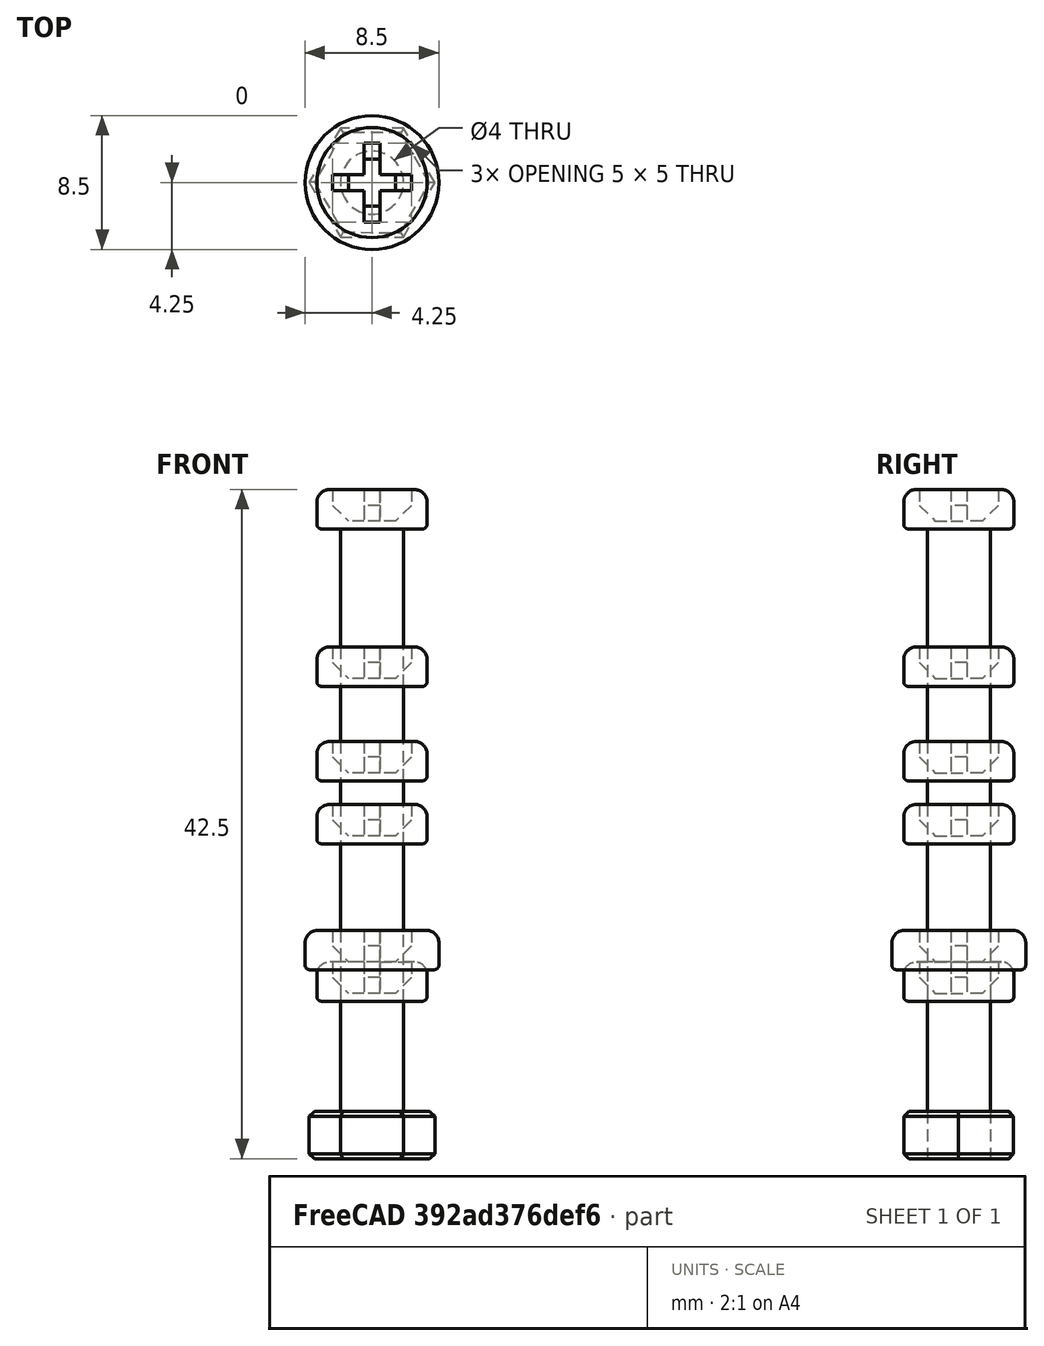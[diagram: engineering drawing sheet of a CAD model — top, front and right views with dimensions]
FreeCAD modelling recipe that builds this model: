
FCSTD DOCUMENT  (FreeCAD 0.18R4 (GitTag))
Label: M4_Screw
License: All rights reserved
LicenseURL: http://en.wikipedia.org/wiki/All_rights_reserved
objects: Sketcher::SketchObject×25, PartDesign::Pad×13, PartDesign::Pocket×12, PartDesign::Fillet×12, PartDesign::Chamfer×8, PartDesign::Body×7
note: 102 computed .brp shape members not serialized (recipe doc carries the construction recipe); baked Part::Feature solids carry a one-line shape summary decoded from their .brp

FEATURE [Sketcher::SketchObject] Sketch
  MapMode = 5
  Support = -> [XY_Plane]
  sketch-geometry (1):
    g0: Circle CenterX=0 CenterY=0 CenterZ=0 NormalX=0 NormalY=0 NormalZ=1 AngleXU=0 Radius=2
  constraints (2):
    c: Coincident(g0,g-1)
    c: Diameter(g0) = 4
FEATURE [PartDesign::Pad] Pad
  Length = 10
  Length2 = 100
  Profile = -> Sketch
  Type = 0
FEATURE [Sketcher::SketchObject] Sketch001
  MapMode = 5
  Placement = pos=(0,0,10) rot=(0,0,1;0rad)
  Support = -> [Pad]
  sketch-geometry (1):
    g0: Circle CenterX=0 CenterY=0 CenterZ=0 NormalX=0 NormalY=0 NormalZ=1 AngleXU=0 Radius=3.5
  constraints (2):
    c: Diameter(g0) = 7
    c: Coincident(g0,g-1)
FEATURE [PartDesign::Pad] Pad001
  BaseFeature = -> Pad
  Length = 2.5
  Length2 = 100
  Profile = -> Sketch001
  Type = 0
FEATURE [Sketcher::SketchObject] Sketch002
  MapMode = 5
  Placement = pos=(0,0,12.5) rot=(0,0,1;0rad)
  Support = -> [Pad001]
  sketch-geometry (4):
    g0: LineSegment StartX=-2.5 StartY=0.5 StartZ=0 EndX=2.5 EndY=0.5 EndZ=0
    g1: LineSegment StartX=2.5 StartY=0.5 StartZ=0 EndX=2.5 EndY=-0.5 EndZ=0
    g2: LineSegment StartX=2.5 StartY=-0.5 StartZ=0 EndX=-2.5 EndY=-0.5 EndZ=0
    g3: LineSegment StartX=-2.5 StartY=-0.5 StartZ=0 EndX=-2.5 EndY=0.5 EndZ=0
  constraints (12):
    c: Coincident(g0,g1)
    c: Coincident(g1,g2)
    c: Coincident(g2,g3)
    c: Coincident(g3,g0)
    c: Horizontal(g0)
    c: Horizontal(g2)
    c: Vertical(g1)
    c: Vertical(g3)
    c: Distance(g1) = 1
    c: Distance(g0) = 5
    c: Distance(g0,g-2) = 2.5
    c: Distance(g0,g-1) = 0.5
FEATURE [PartDesign::Pocket] Pocket
  BaseFeature = -> Pad001
  Length = 2
  Length2 = 100
  Profile = -> Sketch002
  Type = 0
FEATURE [Sketcher::SketchObject] Sketch003
  MapMode = 5
  Placement = pos=(0,0,12.5) rot=(0,0,1;0rad)
  Support = -> [Pocket]
  sketch-geometry (4):
    g0: LineSegment StartX=-0.5 StartY=2.5 StartZ=0 EndX=0.5 EndY=2.5 EndZ=0
    g1: LineSegment StartX=0.5 StartY=2.5 StartZ=0 EndX=0.5 EndY=-2.5 EndZ=0
    g2: LineSegment StartX=0.5 StartY=-2.5 StartZ=0 EndX=-0.5 EndY=-2.5 EndZ=0
    g3: LineSegment StartX=-0.5 StartY=-2.5 StartZ=0 EndX=-0.5 EndY=2.5 EndZ=0
  constraints (12):
    c: Coincident(g0,g1)
    c: Coincident(g1,g2)
    c: Coincident(g2,g3)
    c: Coincident(g3,g0)
    c: Horizontal(g0)
    c: Horizontal(g2)
    c: Vertical(g1)
    c: Vertical(g3)
    c: Distance(g0) = 1
    c: Distance(g1) = 5
    c: Distance(g0,g-1) = 2.5
    c: Distance(g0,g-2) = 0.5
FEATURE [PartDesign::Pocket] Pocket001
  BaseFeature = -> Pocket
  Length = 2
  Length2 = 100
  Profile = -> Sketch003
  Type = 0
FEATURE [PartDesign::Fillet] Fillet
  Base = -> Pocket001 [Edge3]
  BaseFeature = -> Pocket001
  Radius = 0.8
FEATURE [PartDesign::Chamfer] Chamfer
  Base = -> Fillet [Edge33,Edge39,Edge44,Edge27]
  BaseFeature = -> Fillet
  Size = 1
FEATURE [PartDesign::Fillet] Fillet001
  Base = -> Chamfer [Edge55]
  BaseFeature = -> Chamfer
  Radius = 0.3
FEATURE [PartDesign::Body] Body  label="M4_10mm"
  Group = -> [Sketch,Pad,Sketch001,Pad001,Sketch002,Pocket,Sketch003,Pocket001,Fillet,Chamfer,Fillet001]
  Origin = -> Origin
  Tip = -> Fillet001
FEATURE [Sketcher::SketchObject] Sketch004
  MapMode = 5
  Support = -> [XY_Plane001]
  sketch-geometry (8):
    g0: LineSegment StartX=2.01275 StartY=3.45671 StartZ=0 EndX=-1.98722 EndY=3.47145 EndZ=0
    g1: LineSegment StartX=-1.98722 StartY=3.47145 StartZ=0 EndX=-3.99997 EndY=0.0147426 EndZ=0
    g2: LineSegment StartX=-3.99997 StartY=0.0147426 StartZ=0 EndX=-2.01275 EndY=-3.45671 EndZ=0
    g3: LineSegment StartX=-2.01275 StartY=-3.45671 StartZ=0 EndX=1.98722 EndY=-3.47145 EndZ=0
    g4: LineSegment StartX=1.98722 StartY=-3.47145 StartZ=0 EndX=3.99997 EndY=-0.0147426 EndZ=0
    g5: LineSegment StartX=3.99997 StartY=-0.0147426 StartZ=0 EndX=2.01275 EndY=3.45671 EndZ=0
    g6: Circle [constr] CenterX=0 CenterY=0 CenterZ=0 NormalX=0 NormalY=0 NormalZ=1 AngleXU=0 Radius=4
    g7: Circle CenterX=0 CenterY=0 CenterZ=0 NormalX=0 NormalY=0 NormalZ=1 AngleXU=0 Radius=2
  constraints (17):
    c: Coincident(g0,g1)
    c: Coincident(g1,g2)
    c: Coincident(g2,g3)
    c: Coincident(g3,g4)
    c: Coincident(g4,g5)
    c: Coincident(g5,g0)
    c: Equal(g0, g1-g5) x5
    c: PointOnObject(g0,g6)
    c: PointOnObject(g1,g6)
    c: PointOnObject(g2,g6)
    c: PointOnObject(g3,g6)
    c: PointOnObject(g4,g6)
    c: PointOnObject(g5,g6)
    c: Distance(g0) = 4
    c: Coincident(g6,g-1)
    c: Diameter(g7) = 4
    c: Coincident(g7,g-1)
FEATURE [PartDesign::Pad] Pad002
  Length = 3
  Length2 = 100
  Profile = -> Sketch004
  Type = 0
FEATURE [PartDesign::Chamfer] Chamfer001
  Base = -> Pad002 [Edge9,Edge12,Edge15,Edge17,Edge3,Edge6]
  BaseFeature = -> Pad002
  Size = 0.3
FEATURE [PartDesign::Chamfer] Chamfer002
  Base = -> Chamfer001 [Edge13,Edge12,Edge11,Edge3,Edge7,Edge14]
  BaseFeature = -> Chamfer001
  Size = 0.3
FEATURE [PartDesign::Body] Body001  label="M4_Nut"
  Group = -> [Sketch004,Pad002,Chamfer001,Chamfer002]
  Origin = -> Origin001
  Tip = -> Chamfer002
FEATURE [Sketcher::SketchObject] Sketch006
  MapMode = 5
  Support = -> [XY_Plane002]
  sketch-geometry (1):
    g0: Circle CenterX=0 CenterY=0 CenterZ=0 NormalX=0 NormalY=0 NormalZ=1 AngleXU=0 Radius=2
  constraints (2):
    c: Coincident(g0,g-1)
    c: Diameter(g0) = 4
FEATURE [PartDesign::Pad] Pad004
  Length = 30
  Length2 = 100
  Profile = -> Sketch006
  Type = 0
FEATURE [Sketcher::SketchObject] Sketch005
  MapMode = 5
  Placement = pos=(0,0,30) rot=(0,0,1;0rad)
  Support = -> [Pad004]
  sketch-geometry (1):
    g0: Circle CenterX=0 CenterY=0 CenterZ=0 NormalX=0 NormalY=0 NormalZ=1 AngleXU=0 Radius=3.5
  constraints (2):
    c: Diameter(g0) = 7
    c: Coincident(g0,g-1)
FEATURE [PartDesign::Pad] Pad003
  BaseFeature = -> Pad004
  Length = 2.5
  Length2 = 100
  Profile = -> Sketch005
  Type = 0
FEATURE [Sketcher::SketchObject] Sketch008
  MapMode = 5
  Placement = pos=(0,0,32.5) rot=(0,0,1;0rad)
  Support = -> [Pad003]
  sketch-geometry (4):
    g0: LineSegment StartX=-2.5 StartY=0.5 StartZ=0 EndX=2.5 EndY=0.5 EndZ=0
    g1: LineSegment StartX=2.5 StartY=0.5 StartZ=0 EndX=2.5 EndY=-0.5 EndZ=0
    g2: LineSegment StartX=2.5 StartY=-0.5 StartZ=0 EndX=-2.5 EndY=-0.5 EndZ=0
    g3: LineSegment StartX=-2.5 StartY=-0.5 StartZ=0 EndX=-2.5 EndY=0.5 EndZ=0
  constraints (12):
    c: Coincident(g0,g1)
    c: Coincident(g1,g2)
    c: Coincident(g2,g3)
    c: Coincident(g3,g0)
    c: Horizontal(g0)
    c: Horizontal(g2)
    c: Vertical(g1)
    c: Vertical(g3)
    c: Distance(g1) = 1
    c: Distance(g0) = 5
    c: Distance(g0,g-2) = 2.5
    c: Distance(g0,g-1) = 0.5
FEATURE [PartDesign::Pocket] Pocket003
  BaseFeature = -> Pad003
  Length = 2
  Length2 = 100
  Profile = -> Sketch008
  Type = 0
FEATURE [Sketcher::SketchObject] Sketch007
  MapMode = 5
  Placement = pos=(0,0,32.5) rot=(0,0,1;0rad)
  Support = -> [Pocket003]
  sketch-geometry (4):
    g0: LineSegment StartX=-0.5 StartY=2.5 StartZ=0 EndX=0.5 EndY=2.5 EndZ=0
    g1: LineSegment StartX=0.5 StartY=2.5 StartZ=0 EndX=0.5 EndY=-2.5 EndZ=0
    g2: LineSegment StartX=0.5 StartY=-2.5 StartZ=0 EndX=-0.5 EndY=-2.5 EndZ=0
    g3: LineSegment StartX=-0.5 StartY=-2.5 StartZ=0 EndX=-0.5 EndY=2.5 EndZ=0
  constraints (12):
    c: Coincident(g0,g1)
    c: Coincident(g1,g2)
    c: Coincident(g2,g3)
    c: Coincident(g3,g0)
    c: Horizontal(g0)
    c: Horizontal(g2)
    c: Vertical(g1)
    c: Vertical(g3)
    c: Distance(g0) = 1
    c: Distance(g1) = 5
    c: Distance(g0,g-1) = 2.5
    c: Distance(g0,g-2) = 0.5
FEATURE [PartDesign::Pocket] Pocket002
  BaseFeature = -> Pocket003
  Length = 2
  Length2 = 100
  Profile = -> Sketch007
  Type = 0
FEATURE [PartDesign::Fillet] Fillet003
  Base = -> Pocket002 [Edge3]
  BaseFeature = -> Pocket002
  Radius = 0.8
FEATURE [PartDesign::Chamfer] Chamfer003
  Base = -> Fillet003 [Edge33,Edge39,Edge44,Edge27]
  BaseFeature = -> Fillet003
  Size = 1
FEATURE [PartDesign::Fillet] Fillet002
  Base = -> Chamfer003 [Edge55]
  BaseFeature = -> Chamfer003
  Radius = 0.3
FEATURE [PartDesign::Body] Body002  label="M4_30mm"
  Group = -> [Sketch006,Pad004,Sketch005,Pad003,Sketch008,Pocket003,Sketch007,Pocket002,Fillet003,Chamfer003,Fillet002]
  Origin = -> Origin002
  Tip = -> Fillet002
FEATURE [Sketcher::SketchObject] Sketch010
  MapMode = 5
  Support = -> [XY_Plane003]
  sketch-geometry (1):
    g0: Circle CenterX=0 CenterY=0 CenterZ=0 NormalX=0 NormalY=0 NormalZ=1 AngleXU=0 Radius=2
  constraints (2):
    c: Coincident(g0,g-1)
    c: Diameter(g0) = 4
FEATURE [PartDesign::Pad] Pad006
  Length = 24
  Length2 = 100
  Profile = -> Sketch010
  Type = 0
FEATURE [Sketcher::SketchObject] Sketch009
  MapMode = 5
  Placement = pos=(0,0,24) rot=(0,0,1;0rad)
  Support = -> [Pad006]
  sketch-geometry (1):
    g0: Circle CenterX=0 CenterY=0 CenterZ=0 NormalX=0 NormalY=0 NormalZ=1 AngleXU=0 Radius=3.5
  constraints (2):
    c: Diameter(g0) = 7
    c: Coincident(g0,g-1)
FEATURE [PartDesign::Pad] Pad005
  BaseFeature = -> Pad006
  Length = 2.5
  Length2 = 100
  Profile = -> Sketch009
  Type = 0
FEATURE [Sketcher::SketchObject] Sketch012
  MapMode = 5
  Placement = pos=(0,0,26.5) rot=(0,0,1;0rad)
  Support = -> [Pad005]
  sketch-geometry (4):
    g0: LineSegment StartX=-2.5 StartY=0.5 StartZ=0 EndX=2.5 EndY=0.5 EndZ=0
    g1: LineSegment StartX=2.5 StartY=0.5 StartZ=0 EndX=2.5 EndY=-0.5 EndZ=0
    g2: LineSegment StartX=2.5 StartY=-0.5 StartZ=0 EndX=-2.5 EndY=-0.5 EndZ=0
    g3: LineSegment StartX=-2.5 StartY=-0.5 StartZ=0 EndX=-2.5 EndY=0.5 EndZ=0
  constraints (12):
    c: Coincident(g0,g1)
    c: Coincident(g1,g2)
    c: Coincident(g2,g3)
    c: Coincident(g3,g0)
    c: Horizontal(g0)
    c: Horizontal(g2)
    c: Vertical(g1)
    c: Vertical(g3)
    c: Distance(g1) = 1
    c: Distance(g0) = 5
    c: Distance(g0,g-2) = 2.5
    c: Distance(g0,g-1) = 0.5
FEATURE [PartDesign::Pocket] Pocket005
  BaseFeature = -> Pad005
  Length = 2
  Length2 = 100
  Profile = -> Sketch012
  Type = 0
FEATURE [Sketcher::SketchObject] Sketch011
  MapMode = 5
  Placement = pos=(0,0,26.5) rot=(0,0,1;0rad)
  Support = -> [Pocket005]
  sketch-geometry (4):
    g0: LineSegment StartX=-0.5 StartY=2.5 StartZ=0 EndX=0.5 EndY=2.5 EndZ=0
    g1: LineSegment StartX=0.5 StartY=2.5 StartZ=0 EndX=0.5 EndY=-2.5 EndZ=0
    g2: LineSegment StartX=0.5 StartY=-2.5 StartZ=0 EndX=-0.5 EndY=-2.5 EndZ=0
    g3: LineSegment StartX=-0.5 StartY=-2.5 StartZ=0 EndX=-0.5 EndY=2.5 EndZ=0
  constraints (12):
    c: Coincident(g0,g1)
    c: Coincident(g1,g2)
    c: Coincident(g2,g3)
    c: Coincident(g3,g0)
    c: Horizontal(g0)
    c: Horizontal(g2)
    c: Vertical(g1)
    c: Vertical(g3)
    c: Distance(g0) = 1
    c: Distance(g1) = 5
    c: Distance(g0,g-1) = 2.5
    c: Distance(g0,g-2) = 0.5
FEATURE [PartDesign::Pocket] Pocket004
  BaseFeature = -> Pocket005
  Length = 2
  Length2 = 100
  Profile = -> Sketch011
  Type = 0
FEATURE [PartDesign::Fillet] Fillet005
  Base = -> Pocket004 [Edge3]
  BaseFeature = -> Pocket004
  Radius = 0.8
FEATURE [PartDesign::Chamfer] Chamfer004
  Base = -> Fillet005 [Edge33,Edge39,Edge44,Edge27]
  BaseFeature = -> Fillet005
  Size = 1
FEATURE [PartDesign::Fillet] Fillet004
  Base = -> Chamfer004 [Edge55]
  BaseFeature = -> Chamfer004
  Radius = 0.3
FEATURE [PartDesign::Body] Body003  label="M4_24mm"
  Group = -> [Sketch010,Pad006,Sketch009,Pad005,Sketch012,Pocket005,Sketch011,Pocket004,Fillet005,Chamfer004,Fillet004]
  Origin = -> Origin003
  Tip = -> Fillet004
FEATURE [Sketcher::SketchObject] Sketch013
  MapMode = 5
  Support = -> [XY_Plane004]
  sketch-geometry (1):
    g0: Circle CenterX=0 CenterY=0 CenterZ=0 NormalX=0 NormalY=0 NormalZ=1 AngleXU=0 Radius=2
  constraints (2):
    c: Coincident(g0,g-1)
    c: Diameter(g0) = 4
FEATURE [PartDesign::Pad] Pad008
  Length = 40
  Length2 = 100
  Profile = -> Sketch013
  Type = 0
FEATURE [Sketcher::SketchObject] Sketch014
  MapMode = 5
  Placement = pos=(0,0,40) rot=(0,0,1;0rad)
  Support = -> [Pad008]
  sketch-geometry (1):
    g0: Circle CenterX=0 CenterY=0 CenterZ=0 NormalX=0 NormalY=0 NormalZ=1 AngleXU=0 Radius=3.5
  constraints (2):
    c: Diameter(g0) = 7
    c: Coincident(g0,g-1)
FEATURE [PartDesign::Pad] Pad007
  BaseFeature = -> Pad008
  Length = 2.5
  Length2 = 100
  Profile = -> Sketch014
  Type = 0
FEATURE [Sketcher::SketchObject] Sketch016
  MapMode = 5
  Placement = pos=(0,0,42.5) rot=(0,0,1;0rad)
  Support = -> [Pad007]
  sketch-geometry (4):
    g0: LineSegment StartX=-2.5 StartY=0.5 StartZ=0 EndX=2.5 EndY=0.5 EndZ=0
    g1: LineSegment StartX=2.5 StartY=0.5 StartZ=0 EndX=2.5 EndY=-0.5 EndZ=0
    g2: LineSegment StartX=2.5 StartY=-0.5 StartZ=0 EndX=-2.5 EndY=-0.5 EndZ=0
    g3: LineSegment StartX=-2.5 StartY=-0.5 StartZ=0 EndX=-2.5 EndY=0.5 EndZ=0
  constraints (12):
    c: Coincident(g0,g1)
    c: Coincident(g1,g2)
    c: Coincident(g2,g3)
    c: Coincident(g3,g0)
    c: Horizontal(g0)
    c: Horizontal(g2)
    c: Vertical(g1)
    c: Vertical(g3)
    c: Distance(g1) = 1
    c: Distance(g0) = 5
    c: Distance(g0,g-2) = 2.5
    c: Distance(g0,g-1) = 0.5
FEATURE [PartDesign::Pocket] Pocket006
  BaseFeature = -> Pad007
  Length = 2
  Length2 = 100
  Profile = -> Sketch016
  Type = 0
FEATURE [Sketcher::SketchObject] Sketch015
  MapMode = 5
  Placement = pos=(0,0,42.5) rot=(0,0,1;0rad)
  Support = -> [Pocket006]
  sketch-geometry (4):
    g0: LineSegment StartX=-0.5 StartY=2.5 StartZ=0 EndX=0.5 EndY=2.5 EndZ=0
    g1: LineSegment StartX=0.5 StartY=2.5 StartZ=0 EndX=0.5 EndY=-2.5 EndZ=0
    g2: LineSegment StartX=0.5 StartY=-2.5 StartZ=0 EndX=-0.5 EndY=-2.5 EndZ=0
    g3: LineSegment StartX=-0.5 StartY=-2.5 StartZ=0 EndX=-0.5 EndY=2.5 EndZ=0
  constraints (12):
    c: Coincident(g0,g1)
    c: Coincident(g1,g2)
    c: Coincident(g2,g3)
    c: Coincident(g3,g0)
    c: Horizontal(g0)
    c: Horizontal(g2)
    c: Vertical(g1)
    c: Vertical(g3)
    c: Distance(g0) = 1
    c: Distance(g1) = 5
    c: Distance(g0,g-1) = 2.5
    c: Distance(g0,g-2) = 0.5
FEATURE [PartDesign::Pocket] Pocket007
  BaseFeature = -> Pocket006
  Length = 2
  Length2 = 100
  Profile = -> Sketch015
  Type = 0
FEATURE [PartDesign::Fillet] Fillet006
  Base = -> Pocket007 [Edge3]
  BaseFeature = -> Pocket007
  Radius = 0.8
FEATURE [PartDesign::Chamfer] Chamfer005
  Base = -> Fillet006 [Edge33,Edge39,Edge44,Edge27]
  BaseFeature = -> Fillet006
  Size = 1
FEATURE [PartDesign::Fillet] Fillet007
  Base = -> Chamfer005 [Edge55]
  BaseFeature = -> Chamfer005
  Radius = 0.3
FEATURE [PartDesign::Body] Body004  label="M4_40mm"
  Group = -> [Sketch013,Pad008,Sketch014,Pad007,Sketch016,Pocket006,Sketch015,Pocket007,Fillet006,Chamfer005,Fillet007]
  Origin = -> Origin004
  Tip = -> Fillet007
FEATURE [Sketcher::SketchObject] Sketch018
  MapMode = 5
  Support = -> [XY_Plane005]
  sketch-geometry (1):
    g0: Circle CenterX=0 CenterY=0 CenterZ=0 NormalX=0 NormalY=0 NormalZ=1 AngleXU=0 Radius=2
  constraints (2):
    c: Coincident(g0,g-1)
    c: Diameter(g0) = 4
FEATURE [PartDesign::Pad] Pad010
  Length = 12
  Length2 = 100
  Profile = -> Sketch018
  Type = 0
FEATURE [Sketcher::SketchObject] Sketch017
  MapMode = 5
  Placement = pos=(0,0,12) rot=(0,0,1;0rad)
  Support = -> [Pad010]
  sketch-geometry (1):
    g0: Circle CenterX=0 CenterY=0 CenterZ=0 NormalX=0 NormalY=0 NormalZ=1 AngleXU=0 Radius=4.25
  constraints (2):
    c: Diameter(g0) = 8.5
    c: Coincident(g0,g-1)
FEATURE [PartDesign::Pad] Pad009
  BaseFeature = -> Pad010
  Length = 2.5
  Length2 = 100
  Profile = -> Sketch017
  Type = 0
FEATURE [Sketcher::SketchObject] Sketch020
  MapMode = 5
  Placement = pos=(0,0,14.5) rot=(0,0,1;0rad)
  Support = -> [Pad009]
  sketch-geometry (4):
    g0: LineSegment StartX=-2.5 StartY=0.5 StartZ=0 EndX=2.5 EndY=0.5 EndZ=0
    g1: LineSegment StartX=2.5 StartY=0.5 StartZ=0 EndX=2.5 EndY=-0.5 EndZ=0
    g2: LineSegment StartX=2.5 StartY=-0.5 StartZ=0 EndX=-2.5 EndY=-0.5 EndZ=0
    g3: LineSegment StartX=-2.5 StartY=-0.5 StartZ=0 EndX=-2.5 EndY=0.5 EndZ=0
  constraints (12):
    c: Coincident(g0,g1)
    c: Coincident(g1,g2)
    c: Coincident(g2,g3)
    c: Coincident(g3,g0)
    c: Horizontal(g0)
    c: Horizontal(g2)
    c: Vertical(g1)
    c: Vertical(g3)
    c: Distance(g1) = 1
    c: Distance(g0) = 5
    c: Distance(g0,g-2) = 2.5
    c: Distance(g0,g-1) = 0.5
FEATURE [PartDesign::Pocket] Pocket009
  BaseFeature = -> Pad009
  Length = 2
  Length2 = 100
  Profile = -> Sketch020
  Type = 0
FEATURE [Sketcher::SketchObject] Sketch019
  MapMode = 5
  Placement = pos=(0,0,14.5) rot=(0,0,1;0rad)
  Support = -> [Pocket009]
  sketch-geometry (4):
    g0: LineSegment StartX=-0.5 StartY=2.5 StartZ=0 EndX=0.5 EndY=2.5 EndZ=0
    g1: LineSegment StartX=0.5 StartY=2.5 StartZ=0 EndX=0.5 EndY=-2.5 EndZ=0
    g2: LineSegment StartX=0.5 StartY=-2.5 StartZ=0 EndX=-0.5 EndY=-2.5 EndZ=0
    g3: LineSegment StartX=-0.5 StartY=-2.5 StartZ=0 EndX=-0.5 EndY=2.5 EndZ=0
  constraints (12):
    c: Coincident(g0,g1)
    c: Coincident(g1,g2)
    c: Coincident(g2,g3)
    c: Coincident(g3,g0)
    c: Horizontal(g0)
    c: Horizontal(g2)
    c: Vertical(g1)
    c: Vertical(g3)
    c: Distance(g0) = 1
    c: Distance(g1) = 5
    c: Distance(g0,g-1) = 2.5
    c: Distance(g0,g-2) = 0.5
FEATURE [PartDesign::Pocket] Pocket008
  BaseFeature = -> Pocket009
  Length = 2
  Length2 = 100
  Profile = -> Sketch019
  Type = 0
FEATURE [PartDesign::Fillet] Fillet009
  Base = -> Pocket008 [Edge3]
  BaseFeature = -> Pocket008
  Radius = 0.8
FEATURE [PartDesign::Chamfer] Chamfer006
  Base = -> Fillet009 [Edge33,Edge39,Edge44,Edge27]
  BaseFeature = -> Fillet009
  Size = 1
FEATURE [PartDesign::Fillet] Fillet008
  Base = -> Chamfer006 [Edge55]
  BaseFeature = -> Chamfer006
  Radius = 0.3
FEATURE [PartDesign::Body] Body005  label="M4_12mm"
  Group = -> [Sketch018,Pad010,Sketch017,Pad009,Sketch020,Pocket009,Sketch019,Pocket008,Fillet009,Chamfer006,Fillet008]
  Origin = -> Origin005
  Tip = -> Fillet008
FEATURE [Sketcher::SketchObject] Sketch021
  MapMode = 5
  Support = -> [XY_Plane006]
  sketch-geometry (1):
    g0: Circle CenterX=0 CenterY=0 CenterZ=0 NormalX=0 NormalY=0 NormalZ=1 AngleXU=0 Radius=2
  constraints (2):
    c: Coincident(g0,g-1)
    c: Diameter(g0) = 4
FEATURE [PartDesign::Pad] Pad012
  Length = 20
  Length2 = 100
  Profile = -> Sketch021
  Type = 0
FEATURE [Sketcher::SketchObject] Sketch024
  MapMode = 5
  Placement = pos=(0,0,20) rot=(0,0,1;0rad)
  Support = -> [Pad012]
  sketch-geometry (1):
    g0: Circle CenterX=0 CenterY=0 CenterZ=0 NormalX=0 NormalY=0 NormalZ=1 AngleXU=0 Radius=3.5
  constraints (2):
    c: Diameter(g0) = 7
    c: Coincident(g0,g-1)
FEATURE [PartDesign::Pad] Pad011
  BaseFeature = -> Pad012
  Length = 2.5
  Length2 = 100
  Profile = -> Sketch024
  Type = 0
FEATURE [Sketcher::SketchObject] Sketch022
  MapMode = 5
  Placement = pos=(0,0,22.5) rot=(0,0,1;0rad)
  Support = -> [Pad011]
  sketch-geometry (4):
    g0: LineSegment StartX=-2.5 StartY=0.5 StartZ=0 EndX=2.5 EndY=0.5 EndZ=0
    g1: LineSegment StartX=2.5 StartY=0.5 StartZ=0 EndX=2.5 EndY=-0.5 EndZ=0
    g2: LineSegment StartX=2.5 StartY=-0.5 StartZ=0 EndX=-2.5 EndY=-0.5 EndZ=0
    g3: LineSegment StartX=-2.5 StartY=-0.5 StartZ=0 EndX=-2.5 EndY=0.5 EndZ=0
  constraints (12):
    c: Coincident(g0,g1)
    c: Coincident(g1,g2)
    c: Coincident(g2,g3)
    c: Coincident(g3,g0)
    c: Horizontal(g0)
    c: Horizontal(g2)
    c: Vertical(g1)
    c: Vertical(g3)
    c: Distance(g1) = 1
    c: Distance(g0) = 5
    c: Distance(g0,g-2) = 2.5
    c: Distance(g0,g-1) = 0.5
FEATURE [PartDesign::Pocket] Pocket011
  BaseFeature = -> Pad011
  Length = 2
  Length2 = 100
  Profile = -> Sketch022
  Type = 0
FEATURE [Sketcher::SketchObject] Sketch023
  MapMode = 5
  Placement = pos=(0,0,22.5) rot=(0,0,1;0rad)
  Support = -> [Pocket011]
  sketch-geometry (4):
    g0: LineSegment StartX=-0.5 StartY=2.5 StartZ=0 EndX=0.5 EndY=2.5 EndZ=0
    g1: LineSegment StartX=0.5 StartY=2.5 StartZ=0 EndX=0.5 EndY=-2.5 EndZ=0
    g2: LineSegment StartX=0.5 StartY=-2.5 StartZ=0 EndX=-0.5 EndY=-2.5 EndZ=0
    g3: LineSegment StartX=-0.5 StartY=-2.5 StartZ=0 EndX=-0.5 EndY=2.5 EndZ=0
  constraints (12):
    c: Coincident(g0,g1)
    c: Coincident(g1,g2)
    c: Coincident(g2,g3)
    c: Coincident(g3,g0)
    c: Horizontal(g0)
    c: Horizontal(g2)
    c: Vertical(g1)
    c: Vertical(g3)
    c: Distance(g0) = 1
    c: Distance(g1) = 5
    c: Distance(g0,g-1) = 2.5
    c: Distance(g0,g-2) = 0.5
FEATURE [PartDesign::Pocket] Pocket010
  BaseFeature = -> Pocket011
  Length = 2
  Length2 = 100
  Profile = -> Sketch023
  Type = 0
FEATURE [PartDesign::Fillet] Fillet011
  Base = -> Pocket010 [Edge3]
  BaseFeature = -> Pocket010
  Radius = 0.8
FEATURE [PartDesign::Chamfer] Chamfer007
  Base = -> Fillet011 [Edge33,Edge39,Edge44,Edge27]
  BaseFeature = -> Fillet011
  Size = 1
FEATURE [PartDesign::Fillet] Fillet010
  Base = -> Chamfer007 [Edge55]
  BaseFeature = -> Chamfer007
  Radius = 0.3
FEATURE [PartDesign::Body] Body006  label="M4_20mm"
  Group = -> [Sketch021,Pad012,Sketch024,Pad011,Sketch022,Pocket011,Sketch023,Pocket010,Fillet011,Chamfer007,Fillet010]
  Origin = -> Origin006
  Tip = -> Fillet010
